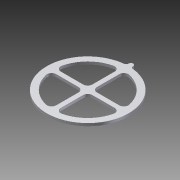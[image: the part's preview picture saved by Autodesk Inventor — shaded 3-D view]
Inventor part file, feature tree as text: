
AUTODESK INVENTOR PART (.ipt)
format: ipt  version: 2012 (Build 160160000, 160)  size: 136,192 bytes
history: native  units: mm
features: extrude x1, sketch x1
ambient origin geometry x8: Origin, YZ Plane, XZ Plane, XY Plane, X Axis, Y Axis, Z Axis, Center Point
bodies: Solid1 (feature_tree)
feature tree (2):
  extrude  "Extrusion1"  Depth=76.2mm
  sketch  "Sketch1"  dims[d0=90.0mm d1=76.2mm d2=2.5mm d3=2.5mm d4=2.5mm d5=2.5mm d6=2.5mm d7=2.5mm d8=2.5mm d9=2.5mm d10=5.0mm d11=5.0mm d12=5.0mm d13=5.0mm d14=38.1mm d15=38.1mm d16=38.1mm d17=38.1mm d18=5.0mm d19=5.0mm d20=50.0mm d21=2.5mm d22=3.0mm d23=0.0mm]
